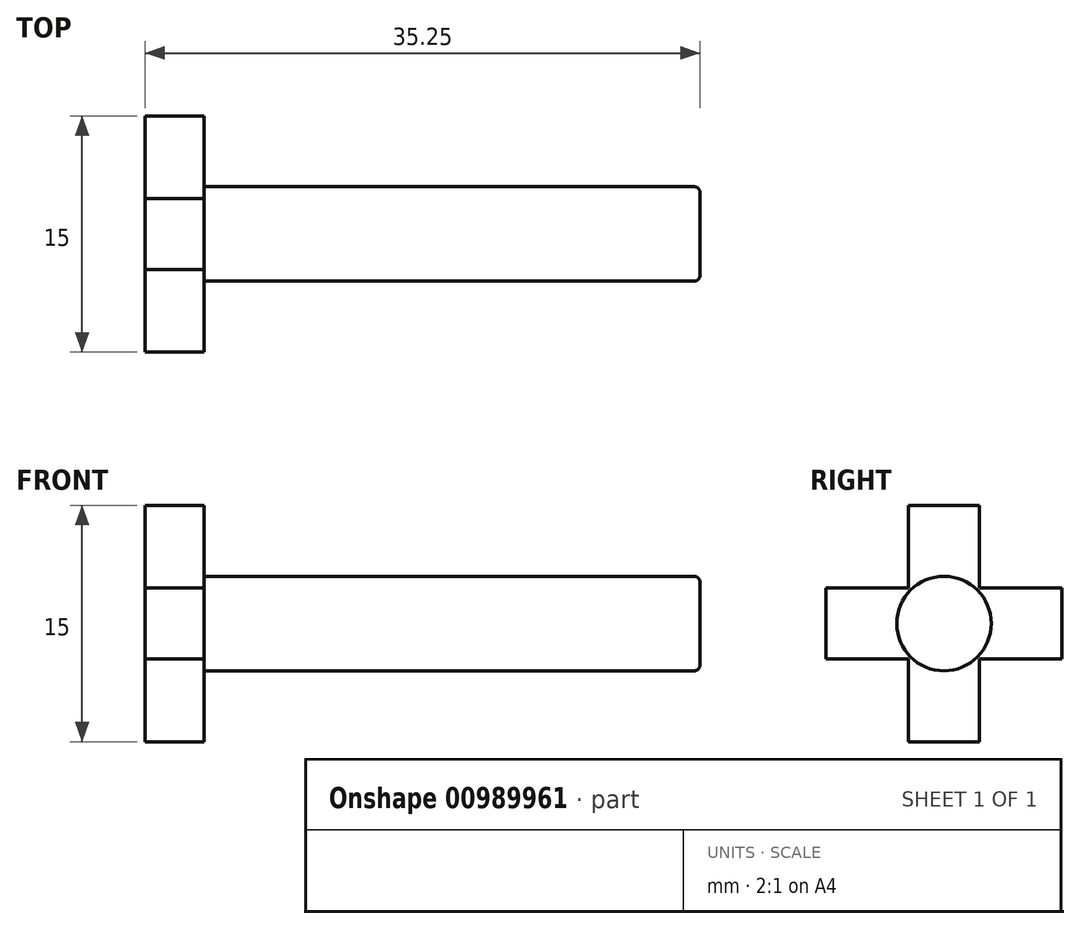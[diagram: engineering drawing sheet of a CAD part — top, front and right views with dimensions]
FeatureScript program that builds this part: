
annotation { "Feature Type Name" : "Feature", "Feature Type Description" : "" }
export const myFeature = defineFeature(function(context is Context, id is Id, definition is map)
    precondition{}
    {
        {
            var Q0;
            Q0=qCreatedBy(makeId("Right.planeOp"),FACE);
            var sketch = newSketch(context, id + "F0", { "sketchPlane" : qUnion([Q0])});
            skCircle(sketch, "E0", {"center": v(0, 0) * mm, "radius": 2 * mm});
            skSolve(sketch);
        }
        {
            var Q0;
            Q0 = qSketchRegion(id + "F0", true);
            extrude(context, id + "F1", {"entities" : qUnion([Q0]), "depth" : 23.5 * mm, "offsetDistance" : 25 * mm});
        }
        {
            var Q0;
            Q0=makeQuery(id+"F1.opExtrude","CAP_FACE",FACE,{"disambiguationData":[OSD([sQuery(id+"F0.wireOp",EDGE,"E0")])],"isStart":true});
            var sketch = newSketch(context, id + "F2", { "sketchPlane" : qUnion([Q0])});
            skLineSegment(sketch, "E1", {"start": v(0, 0) * mm, "end": v(0, 5) * mm, "construction": true});
            skLineSegment(sketch, "E2", {"start": v(0, 0) * mm, "end": v(0, -5) * mm, "construction": true});
            skLineSegment(sketch, "E3", {"start": v(0, 0) * mm, "end": v(5, 0) * mm, "construction": true});
            skLineSegment(sketch, "E4", {"start": v(0, 0) * mm, "end": v(-5, 0) * mm, "construction": true});
            skLineSegment(sketch, "E5", {"start": v(0, 5) * mm, "end": v(-1.5, 5) * mm});
            skLineSegment(sketch, "E6.MirrorCS", {"start": v(0, 5) * mm, "end": v(1.5, 5) * mm});
            skLineSegment(sketch, "E7", {"start": v(0, 0) * mm, "end": v(4.77, 4.77) * mm, "construction": true});
            skLineSegment(sketch, "E8.MirrorCS", {"start": v(5, 0) * mm, "end": v(5, 1.5) * mm});
            skLineSegment(sketch, "E9.MirrorCS", {"start": v(0, -5) * mm, "end": v(-1.5, -5) * mm});
            skLineSegment(sketch, "E10.MirrorCS", {"start": v(0, -5) * mm, "end": v(1.5, -5) * mm});
            skLineSegment(sketch, "E11.MirrorCS", {"start": v(5, 0) * mm, "end": v(5, -1.5) * mm});
            skLineSegment(sketch, "E12.MirrorCS", {"start": v(-5, 0) * mm, "end": v(-5, -1.5) * mm});
            skLineSegment(sketch, "E13.MirrorCS", {"start": v(-5, 0) * mm, "end": v(-5, 1.5) * mm});
            skLineSegment(sketch, "E14", {"start": v(-1.5, 5) * mm, "end": v(-1.5, 1.5) * mm});
            skLineSegment(sketch, "E15", {"start": v(1.5, 5) * mm, "end": v(1.5, 1.5) * mm});
            skLineSegment(sketch, "E16", {"start": v(-5, 1.5) * mm, "end": v(-1.5, 1.5) * mm});
            skLineSegment(sketch, "E17", {"start": v(-5, -1.5) * mm, "end": v(-1.5, -1.5) * mm});
            skLineSegment(sketch, "E18.trimOffspring", {"start": v(-1.5, -1.5) * mm, "end": v(-1.5, -5) * mm});
            skLineSegment(sketch, "E19.trimOffspring", {"start": v(1.5, -1.5) * mm, "end": v(1.5, -5) * mm});
            skLineSegment(sketch, "E20.trimOffspring", {"start": v(1.5, 1.5) * mm, "end": v(5, 1.5) * mm});
            skLineSegment(sketch, "E21.trimOffspring", {"start": v(1.5, -1.5) * mm, "end": v(5, -1.5) * mm});
            skSolve(sketch);
        }
        {
            var Q0;
            Q0=makeQuery(id+"F2.imprint","IMPRINT",FACE,{"disambiguationData":[TD([[makeQuery(id+"F2.imprint","IMPRINT",EDGE,{"derivedFrom":sQuery(id+"F2.wireOp",EDGE,"E5")}),1.0]])]});
            extrude(context, id + "F3", {"entities" : qUnion([Q0]), "operationType" : NewBodyOperationType.ADD, "oppositeDirection" : true, "depth" : 2.5 * mm, "offsetDistance" : 25 * mm});
        }
        {
            var Q0;
            Q0=makeQuery(id+"F3.opExtrude","CAP_EDGE",EDGE,{"disambiguationData":[OSD([sQuery(id+"F0.wireOp",EDGE,"E0")])],"isStart":false});
            var Q1;
            Q1=makeQuery(id+"F1.opExtrude","CAP_EDGE",EDGE,{"disambiguationData":[OSD([sQuery(id+"F0.wireOp",EDGE,"E0")])],"isStart":false});
            fillet(context, id + "F4", {"entities" : qUnion([Q0, Q1]), "radius" : .25 * mm, "tangentPropagation" : true, "allowEdgeOverflow" : false});
        }
        {
            var Q0;
            Q0=makeQuery(id+"F1.opExtrude","SWEPT_BODY",BODY,{"disambiguationData":[OSD([sQuery(id+"F0.wireOp",EDGE,"E0")])]});
            var Q1;
            Q1=qCreatedBy(makeId("Origin.pointOp"),VERTEX);
            transform(context, id + "F5", {"entities" : qUnion([Q0]), "transformType" : TransformType.SCALE_UNIFORMLY, "scale" : 1.5, "scalePoint" : qUnion([Q1]), "makeCopy" : false});
        }
    });
